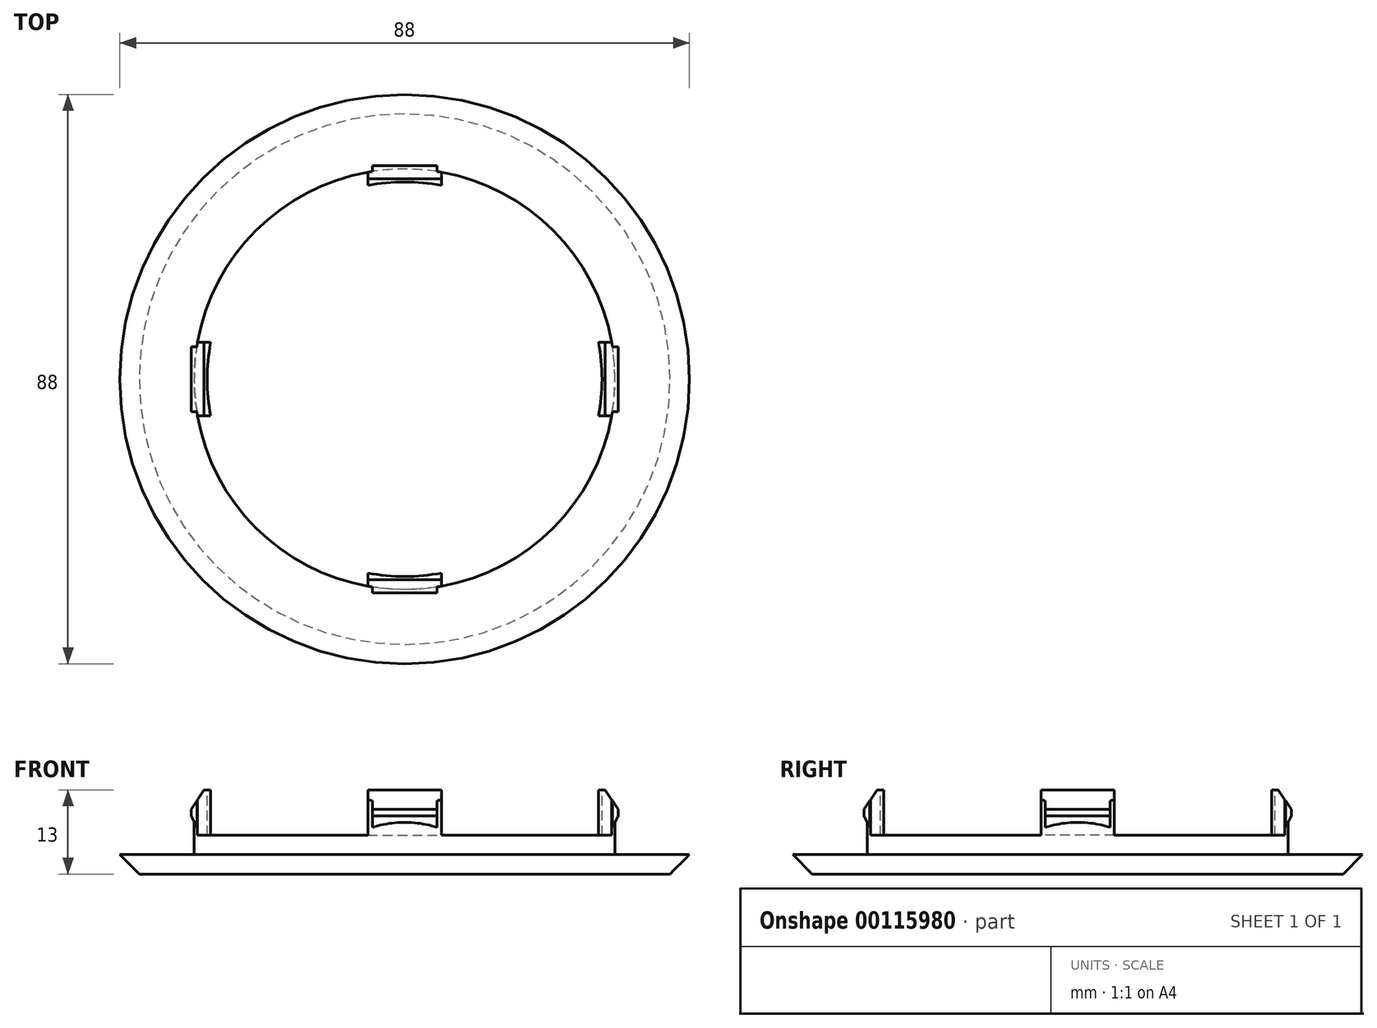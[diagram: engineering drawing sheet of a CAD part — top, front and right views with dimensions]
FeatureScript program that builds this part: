
annotation { "Feature Type Name" : "Feature", "Feature Type Description" : "" }
export const myFeature = defineFeature(function(context is Context, id is Id, definition is map)
    precondition{}
    {
        {
            var Q0;
            Q0=qCreatedBy(makeId("Top.planeOp"),FACE);
            var sketch = newSketch(context, id + "F0", { "sketchPlane" : qUnion([Q0])});
            skCircle(sketch, "E0", {"center": v(0, 0) * mm, "radius": 41 * mm});
            skSolve(sketch);
        }
        {
            var Q0;
            Q0=makeQuery(id+"F0.imprint","IMPRINT",FACE,{"disambiguationData":[TD([[makeQuery(id+"F0.imprint","IMPRINT",EDGE,{"derivedFrom":sQuery(id+"F0.wireOp",EDGE,"E0")}),1.0]])]});
            extrude(context, id + "F1", {"entities" : qUnion([Q0]), "depth" : 3 * mm, "hasDraft" : true, "draftAngle" : 45 * degree});
        }
        {
            var Q0;
            Q0=makeQuery(id+"F1.opExtrude","CAP_FACE",FACE,{"disambiguationData":[OSD([sQuery(id+"F0.wireOp",EDGE,"E0")])],"isStart":false});
            var sketch = newSketch(context, id + "F2", { "sketchPlane" : qUnion([Q0])});
            skCircle(sketch, "E1", {"center": v(0, 0) * mm, "radius": 32.5 * mm});
            skSolve(sketch);
        }
        {
            var Q0;
            Q0 = qSketchRegion(id + "F2", true);
            extrude(context, id + "F3", {"entities" : qUnion([Q0]), "operationType" : NewBodyOperationType.ADD, "depth" : 10 * mm});
        }
        {
            var Q0;
            Q0=qCreatedBy(makeId("Front.planeOp"),FACE);
            var sketch = newSketch(context, id + "F4", { "sketchPlane" : qUnion([Q0])});
            skLineSegment(sketch, "E2.bottom", {"start": v(-5, 7) * mm, "end": v(5, 7) * mm});
            skLineSegment(sketch, "E2.top", {"start": v(-5, 13) * mm, "end": v(5, 13) * mm});
            skLineSegment(sketch, "E2.left", {"start": v(-5, 7) * mm, "end": v(-5, 13) * mm});
            skLineSegment(sketch, "E2.right", {"start": v(5, 7) * mm, "end": v(5, 13) * mm});
            skPoint(sketch, "E2.middle", {"position": v(0, 10) * mm});
            skSolve(sketch);
        }
        {
            var Q0;
            Q0=makeQuery(id+"F3.opExtrude","CAP_FACE",FACE,{"disambiguationData":[OSD([sQuery(id+"F2.wireOp",EDGE,"E1")])],"isStart":false});
            var sketch = newSketch(context, id + "F5", { "sketchPlane" : qUnion([Q0])});
            skCircle(sketch, "E3", {"center": v(0, 0) * mm, "radius": 30.5 * mm});
            skSolve(sketch);
        }
        {
            var Q0;
            Q0 = qSketchRegion(id + "F4", true);
            extrude(context, id + "F6", {"entities" : qUnion([Q0]), "operationType" : NewBodyOperationType.ADD, "depth" : 33 * mm, "hasSecondDirection" : true, "secondDirectionOppositeDirection" : true, "secondDirectionDepth" : 33 * mm});
        }
        {
            var Q0;
            Q0=qCreatedBy(makeId("Right.planeOp"),FACE);
            var sketch = newSketch(context, id + "F7", { "sketchPlane" : qUnion([Q0])});
            skLineSegment(sketch, "E4.bottom", {"start": v(5, 7) * mm, "end": v(-5, 7) * mm});
            skLineSegment(sketch, "E4.top", {"start": v(5, 13) * mm, "end": v(-5, 13) * mm});
            skLineSegment(sketch, "E4.left", {"start": v(5, 7) * mm, "end": v(5, 13) * mm});
            skLineSegment(sketch, "E4.right", {"start": v(-5, 7) * mm, "end": v(-5, 13) * mm});
            skPoint(sketch, "E4.middle", {"position": v(0, 10) * mm});
            skSolve(sketch);
        }
        {
            var Q0;
            Q0 = qSketchRegion(id + "F7", true);
            extrude(context, id + "F8", {"entities" : qUnion([Q0]), "operationType" : NewBodyOperationType.ADD, "depth" : 33 * mm, "hasSecondDirection" : true, "secondDirectionOppositeDirection" : true, "secondDirectionDepth" : 33 * mm});
        }
        {
            var Q0;
            Q0=makeQuery(id+"F5.imprint","IMPRINT",FACE,{"disambiguationData":[TD([[makeQuery(id+"F5.imprint","IMPRINT",EDGE,{"derivedFrom":sQuery(id+"F5.wireOp",EDGE,"E3")}),1.0]])]});
            extrude(context, id + "F9", {"entities" : qUnion([Q0]), "operationType" : NewBodyOperationType.REMOVE, "oppositeDirection" : true, "depth" : 7 * mm});
        }
        {
            var Q0;
            Q0=makeQuery(id+"F8.boolean.opBoolean","MERGE",FACE,{"derivedFrom":[makeQuery(id+"F6.boolean.opBoolean","MERGE",FACE,{"derivedFrom":[makeQuery(id+"F3.opExtrude","CAP_FACE",FACE,{"disambiguationData":[OSD([sQuery(id+"F2.wireOp",EDGE,"E1")])],"isStart":false}),makeQuery(id+"F6.opExtrude","SWEPT_FACE",FACE,{"disambiguationData":[OSD([sQuery(id+"F4.wireOp",EDGE,"E2.top")])]})]}),makeQuery(id+"F8.opExtrude","SWEPT_FACE",FACE,{"disambiguationData":[OSD([sQuery(id+"F7.wireOp",EDGE,"E4.top")])]})]});
            var sketch = newSketch(context, id + "F10", { "sketchPlane" : qUnion([Q0])});
            skCircle(sketch, "E5", {"center": v(0, 0) * mm, "radius": 30 * mm});
            skSolve(sketch);
        }
        {
            var Q0;
            Q0=makeQuery(id+"F8.boolean.opBoolean","MERGE",FACE,{"derivedFrom":[makeQuery(id+"F6.boolean.opBoolean","MERGE",FACE,{"derivedFrom":[makeQuery(id+"F3.opExtrude","CAP_FACE",FACE,{"disambiguationData":[OSD([sQuery(id+"F2.wireOp",EDGE,"E1")])],"isStart":false}),makeQuery(id+"F6.opExtrude","SWEPT_FACE",FACE,{"disambiguationData":[OSD([sQuery(id+"F4.wireOp",EDGE,"E2.top")])]})]}),makeQuery(id+"F8.opExtrude","SWEPT_FACE",FACE,{"disambiguationData":[OSD([sQuery(id+"F7.wireOp",EDGE,"E4.top")])]})]});
            var sketch = newSketch(context, id + "F11", { "sketchPlane" : qUnion([Q0])});
            skLineSegment(sketch, "E6", {"start": v(-32, 5.68) * mm, "end": v(-28.95, 5.68) * mm});
            skLineSegment(sketch, "E7", {"start": v(-32, -5.68) * mm, "end": v(-28.95, -5.68) * mm});
            skLineSegment(sketch, "E8", {"start": v(32, 5.68) * mm, "end": v(28.95, 5.68) * mm});
            skLineSegment(sketch, "E9", {"start": v(32, -5.68) * mm, "end": v(28.95, -5.68) * mm});
            skLineSegment(sketch, "E10", {"start": v(-5.68, -32) * mm, "end": v(-5.68, -28.95) * mm});
            skLineSegment(sketch, "E11", {"start": v(5.68, -32) * mm, "end": v(5.68, -28.95) * mm});
            skLineSegment(sketch, "E12", {"start": v(-5.68, 32) * mm, "end": v(-5.68, 28.95) * mm});
            skLineSegment(sketch, "E13", {"start": v(5.68, 32) * mm, "end": v(5.68, 28.95) * mm});
            skSolve(sketch);
        }
        {
            var Q0;
            Q0 = qSketchRegion(id + "F11", true);
            var Q1;
            {var subQ0=sQuery(id+"F11.wireOp",EDGE,"E6");Q1=makeQuery(id+"F11.imprint","IMPRINT",FACE,{"disambiguationData":[TD([[makeQuery(id+"F11.imprint","IMPRINT",EDGE,{"derivedFrom":subQ0}),1.0]])]});}
            var Q2;
            {var subQ0=sQuery(id+"F11.wireOp",EDGE,"E8");Q2=makeQuery(id+"F11.imprint","IMPRINT",FACE,{"disambiguationData":[TD([[makeQuery(id+"F11.imprint","IMPRINT",EDGE,{"derivedFrom":subQ0}),-1.0]])]});}
            var Q3;
            {var subQ0=sQuery(id+"F11.wireOp",EDGE,"E9");Q3=makeQuery(id+"F11.imprint","IMPRINT",FACE,{"disambiguationData":[TD([[makeQuery(id+"F11.imprint","IMPRINT",EDGE,{"derivedFrom":subQ0}),1.0]])]});}
            var Q4;
            {var subQ0=sQuery(id+"F11.wireOp",EDGE,"E7");Q4=makeQuery(id+"F11.imprint","IMPRINT",FACE,{"disambiguationData":[TD([[makeQuery(id+"F11.imprint","IMPRINT",EDGE,{"derivedFrom":subQ0}),-1.0]])]});}
            extrude(context, id + "F12", {"entities" : qUnion([Q0, Q1, Q2, Q3, Q4]), "operationType" : NewBodyOperationType.REMOVE, "oppositeDirection" : true, "depth" : 7 * mm});
        }
        {
            var Q0;
            Q0=makeQuery(id+"F6.opExtrude","CAP_EDGE",EDGE,{"disambiguationData":[OSD([sQuery(id+"F4.wireOp",EDGE,"E2.top")])],"isStart":true});
            var Q1;
            Q1=makeQuery(id+"F8.opExtrude","CAP_EDGE",EDGE,{"disambiguationData":[OSD([sQuery(id+"F7.wireOp",EDGE,"E4.top")])],"isStart":false});
            chamfer(context, id + "F13", {"entities" : qUnion([Q0, Q1]), "chamferType" : ChamferType.TWO_OFFSETS, "width1" : 3 * mm, "oppositeDirection" : false, "width2" : 2 * mm, "tangentPropagation" : true});
        }
        {
            var Q0;
            Q0=makeQuery(id+"F6.opExtrude","CAP_EDGE",EDGE,{"disambiguationData":[OSD([sQuery(id+"F4.wireOp",EDGE,"E2.top")])],"isStart":false});
            var Q1;
            Q1=makeQuery(id+"F8.opExtrude","CAP_EDGE",EDGE,{"disambiguationData":[OSD([sQuery(id+"F7.wireOp",EDGE,"E4.top")])],"isStart":true});
            chamfer(context, id + "F14", {"entities" : qUnion([Q0, Q1]), "chamferType" : ChamferType.TWO_OFFSETS, "width1" : 2 * mm, "oppositeDirection" : false, "width2" : 3 * mm, "tangentPropagation" : true});
        }
        {
            var Q0;
            Q0=makeQuery(id+"F8.opExtrude","CAP_EDGE",EDGE,{"disambiguationData":[OSD([sQuery(id+"F7.wireOp",EDGE,"E4.bottom")])],"isStart":false});
            var Q1;
            Q1=makeQuery(id+"F6.opExtrude","CAP_EDGE",EDGE,{"disambiguationData":[OSD([sQuery(id+"F4.wireOp",EDGE,"E2.bottom")])],"isStart":true});
            chamfer(context, id + "F15", {"entities" : qUnion([Q0, Q1]), "chamferType" : ChamferType.TWO_OFFSETS, "width1" : 1 * mm, "oppositeDirection" : false, "width2" : 2 * mm, "tangentPropagation" : true});
        }
        {
            var Q0;
            Q0=makeQuery(id+"F6.opExtrude","CAP_EDGE",EDGE,{"disambiguationData":[OSD([sQuery(id+"F4.wireOp",EDGE,"E2.bottom")])],"isStart":false});
            var Q1;
            Q1=makeQuery(id+"F8.opExtrude","CAP_EDGE",EDGE,{"disambiguationData":[OSD([sQuery(id+"F7.wireOp",EDGE,"E4.bottom")])],"isStart":true});
            chamfer(context, id + "F16", {"entities" : qUnion([Q0, Q1]), "chamferType" : ChamferType.TWO_OFFSETS, "width1" : 2 * mm, "oppositeDirection" : false, "width2" : 1 * mm, "tangentPropagation" : true});
        }
    });
